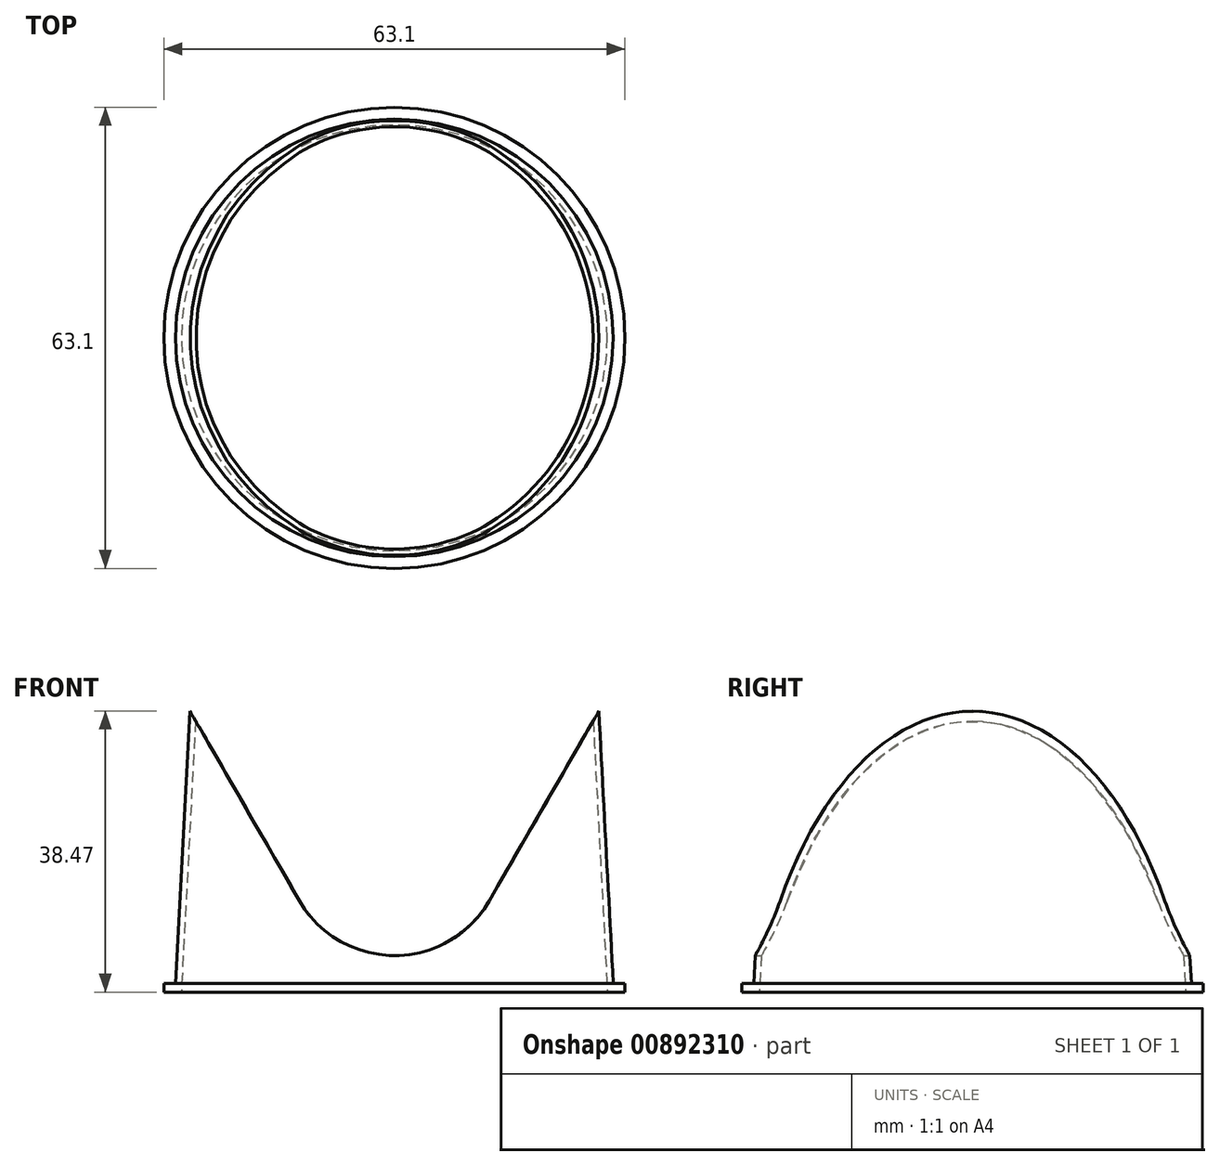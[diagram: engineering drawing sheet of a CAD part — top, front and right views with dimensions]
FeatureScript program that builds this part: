
annotation { "Feature Type Name" : "Feature", "Feature Type Description" : "" }
export const myFeature = defineFeature(function(context is Context, id is Id, definition is map)
    precondition{}
    {
        {
            var Q0;
            Q0=qCreatedBy(makeId("Top.planeOp"),FACE);
            var Q1;
            Q1=qCreatedBy(makeId("Top.planeOp"),FACE);
            var sketch = newSketch(context, id + "F0", { "sketchPlane" : qUnion([Q0, Q1])});
            skCircle(sketch, "E0", {"center": v(0, 0) * mm, "radius": 30 * mm});
            skCircle(sketch, "E1", {"center": v(0, 0) * mm, "radius": 29.16 * mm, "construction": true});
            skSolve(sketch);
        }
        {
            var Q0;
            Q0=makeQuery(id+"F0.imprint","IMPRINT",FACE,{"disambiguationData":[TD([[makeQuery(id+"F0.imprint","IMPRINT",EDGE,{"derivedFrom":sQuery(id+"F0.wireOp",EDGE,"E0")}),1.0]])]});
            extrude(context, id + "F1", {"entities" : qUnion([Q0]), "depth" : 40 * mm, "offsetDistance" : 25 * mm, "hasDraft" : true, "draftAngle" : 3 * degree, "draftPullDirection" : true});
        }
        {
            var Q0;
            Q0=makeQuery(id+"F1.opExtrude","CAP_FACE",FACE,{"disambiguationData":[OSD([sQuery(id+"F0.wireOp",EDGE,"E0")])],"isStart":false});
            var Q1;
            Q1=makeQuery(id+"F1.opExtrude","CAP_FACE",FACE,{"disambiguationData":[OSD([sQuery(id+"F0.wireOp",EDGE,"E0")])],"isStart":true});
            shell(context, id + "F2", {"entities" : qUnion([Q0, Q1]), "thickness" : .85 * mm});
        }
        {
            var Q0;
            Q0=qCreatedBy(makeId("Top.planeOp"),FACE);
            var sketch = newSketch(context, id + "F3", { "sketchPlane" : qUnion([Q0])});
            skCircle(sketch, "E2.0", {"center": v(0, 0) * mm, "radius": 29.15 * mm});
            skCircle(sketch, "E3", {"center": v(0, 0) * mm, "radius": 31.55 * mm});
            skSolve(sketch);
        }
        {
            var Q0;
            Q0=makeQuery(id+"F3.imprint","IMPRINT",FACE,{"disambiguationData":[TD([[makeQuery(id+"F3.imprint","IMPRINT",EDGE,{"derivedFrom":sQuery(id+"F3.wireOp",EDGE,"E3")}),1.0]])]});
            extrude(context, id + "F4", {"entities" : qUnion([Q0]), "operationType" : NewBodyOperationType.ADD, "depth" : 1.2 * mm, "offsetDistance" : 25 * mm});
        }
        {
            var Q0;
            Q0=qCreatedBy(makeId("Front.planeOp"),FACE);
            var sketch = newSketch(context, id + "F5", { "sketchPlane" : qUnion([Q0])});
            skLineSegment(sketch, "E4", {"start": v(0, 0) * mm, "end": v(0, 90.05) * mm, "construction": true});
            skLineSegment(sketch, "E5", {"start": v(-28.87, 40) * mm, "end": v(-13, 12.5) * mm});
            skLineSegment(sketch, "E6", {"start": v(13, 12.5) * mm, "end": v(28.87, 40) * mm});
            skLineSegment(sketch, "E7", {"start": v(-28.87, 40) * mm, "end": v(28.87, 40) * mm});
            skPoint(sketch, "E8.visualSharp", {"position": v(0, -10) * mm});
            skArc(sketch, "E8.filletArc", {"start": v(-13, 12.5) * mm, "mid": v(0, 5) * mm, "end": v(13, 12.5) * mm});
            skSolve(sketch);
        }
        {
            var Q0;
            Q0 = qSketchRegion(id + "F5", true);
            extrude(context, id + "F6", {"entities" : qUnion([Q0]), "operationType" : NewBodyOperationType.REMOVE, "endBound" : BoundingType.SYMMETRIC, "depth" : 65 * mm, "offsetDistance" : 25 * mm});
        }
    });
